# Revit family: ledflood-e3_re144-20w-830-bl-md_709000072400
name_source: partatom
category: Leuchten
revit_build: Autodesk Revit 2016 (Build: 20190508_0715(x64)
units: mm (PartAtom-declared; Revit-internal decimal feet)

## family parameters
Basisbauteil = Fläche
Beim Laden mit Abzugskörper schneiden = Nein
Bemaßung runder Anschluss = Durchmesser verwenden
Gemeinsam genutzt = Nein
Lichtquelle = Nein
Raumberechnungspunkt = Nein
Teiletyp = Normal

## types (1)
- LEDFlood-E3 Re144-20W-830-BL-MD (1 x LED, 2200 lm, 3000)
    Approval mark = CE
    Beschreibung = Equipped with breather to prevent condensation.
    CIE Flux Codes = 52 83 97 100 100
    Color Rendering = 80
    Color Temperature = 3000
    Control Gear = Electronic ballast
    Frequency = 60 Hz
    Height = 34 mm  [stored 0.111549 ft]
    Hersteller = OPPLE
    Lamp Light Flux = 2200 lm
    Lamp count = 1
    Lampe = 1 x LED
    Length = 172 mm
    Luminous efficacy = 110 lm/W
    ModVariant = Nein
    Modell = 709000072400
    Mounting Place = Wall, Pole
    Mounting Type = Surface mounted, Pole top
    Number of Poles = 1
    OnlyDefault = Ja
    Power Factor = 1
    Product Name = LEDFlood-E3 Re144-20W-830-BL-MD
    Product group = Ceiling Light Luna
    ProductGroupID = 305
    Protection Class = Protection class I
    Protection Degree = IP 66
    RLX_Detail_Level = 1
    RlxData = <blob elided: 273777 chars, md5=652ce8e2>
    Scheinlast = 20 VA
    Socket = socket
    Standby Power = 0 W
    System Light Flux = 2200 lm
    System Power = 20 W
    Typenbild = v2_fl_eco_g3_re144_md.jpg
    Typenkommentare = Product without accessories
    URL = http://relux.com
    VarID = ---
    Voltage = 230 V
    Voltage Range = 220-240 V
    Vorgabe-Ansicht = 1800 mm
    Weight = 0.00 kg
    Width = 133 mm  [stored 0.436352 ft]

note: [stored X ft] marks values corroborated as IEEE doubles in the binary element streams (Revit-internal decimal feet)

## geometry (parser evidence)
native form markers: Sweep x14
no freeform markers — native parametric forms only
